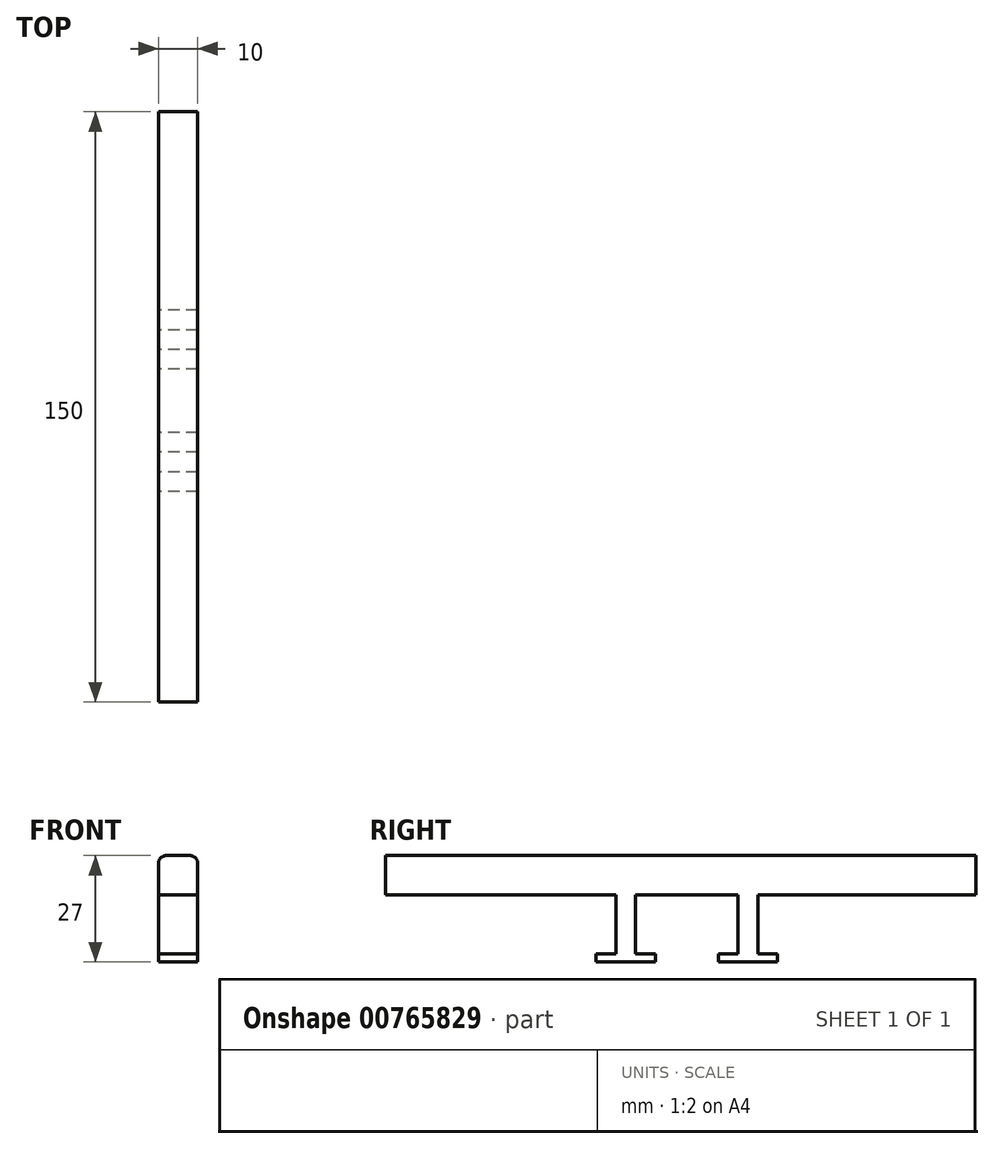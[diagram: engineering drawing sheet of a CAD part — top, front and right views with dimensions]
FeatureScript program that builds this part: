
annotation { "Feature Type Name" : "Feature", "Feature Type Description" : "" }
export const myFeature = defineFeature(function(context is Context, id is Id, definition is map)
    precondition{}
    {
        {
            var Q0;
            Q0=qCreatedBy(makeId("Right.planeOp"),FACE);
            var sketch = newSketch(context, id + "F0", { "sketchPlane" : qUnion([Q0])});
            skLineSegment(sketch, "E0", {"start": v(114.75, -5.85) * mm, "end": v(-35.25, -5.85) * mm});
            skLineSegment(sketch, "E1", {"start": v(23.26, -5.85) * mm, "end": v(23.26, -20.85) * mm});
            skLineSegment(sketch, "E2", {"start": v(-35.25, -5.85) * mm, "end": v(-35.25, 4.15) * mm});
            skLineSegment(sketch, "E3", {"start": v(-35.25, 4.15) * mm, "end": v(114.75, 4.15) * mm});
            skLineSegment(sketch, "E4", {"start": v(114.75, 4.15) * mm, "end": v(114.75, -5.85) * mm});
            skLineSegment(sketch, "E5", {"start": v(23.26, -20.85) * mm, "end": v(18.26, -20.85) * mm});
            skLineSegment(sketch, "E6", {"start": v(18.26, -20.85) * mm, "end": v(28.26, -20.85) * mm});
            skLineSegment(sketch, "E7", {"start": v(28.26, -20.85) * mm, "end": v(28.26, -5.85) * mm});
            skLineSegment(sketch, "E8", {"start": v(28.26, -20.85) * mm, "end": v(33.26, -20.85) * mm});
            skLineSegment(sketch, "E9", {"start": v(18.26, -20.85) * mm, "end": v(18.26, -22.85) * mm});
            skLineSegment(sketch, "E10", {"start": v(18.26, -22.85) * mm, "end": v(33.26, -22.85) * mm});
            skLineSegment(sketch, "E11", {"start": v(33.26, -22.85) * mm, "end": v(33.26, -20.85) * mm});
            skLineSegment(sketch, "E12", {"start": v(54.32, -5.85) * mm, "end": v(54.32, -20.85) * mm});
            skLineSegment(sketch, "E13", {"start": v(54.32, -20.85) * mm, "end": v(49.32, -20.85) * mm});
            skLineSegment(sketch, "E14", {"start": v(49.32, -20.85) * mm, "end": v(49.32, -22.85) * mm});
            skLineSegment(sketch, "E15", {"start": v(49.32, -22.85) * mm, "end": v(64.32, -22.85) * mm});
            skLineSegment(sketch, "E16", {"start": v(54.32, -20.85) * mm, "end": v(59.32, -20.85) * mm});
            skLineSegment(sketch, "E17", {"start": v(59.32, -20.85) * mm, "end": v(59.32, -5.85) * mm});
            skLineSegment(sketch, "E18", {"start": v(59.32, -20.85) * mm, "end": v(64.32, -20.85) * mm});
            skLineSegment(sketch, "E19", {"start": v(64.32, -20.85) * mm, "end": v(64.32, -22.85) * mm});
            skSolve(sketch);
        }
        {
            var Q0;
            Q0 = qSketchRegion(id + "F0", true);
            extrude(context, id + "F1", {"entities" : qUnion([Q0]), "depth" : 10 * mm, "offsetDistance" : 25 * mm});
        }
        {
            var Q0;
            Q0=makeQuery(id+"F1.opExtrude","CAP_EDGE",EDGE,{"disambiguationData":[OSD([sQuery(id+"F0.wireOp",EDGE,"E3")])],"isStart":false});
            var Q1;
            Q1=makeQuery(id+"F1.opExtrude","CAP_EDGE",EDGE,{"disambiguationData":[OSD([sQuery(id+"F0.wireOp",EDGE,"E3")])],"isStart":true});
            fillet(context, id + "F2", {"entities" : qUnion([Q0, Q1]), "radius" : 2 * mm, "tangentPropagation" : true, "allowEdgeOverflow" : false});
        }
    });
